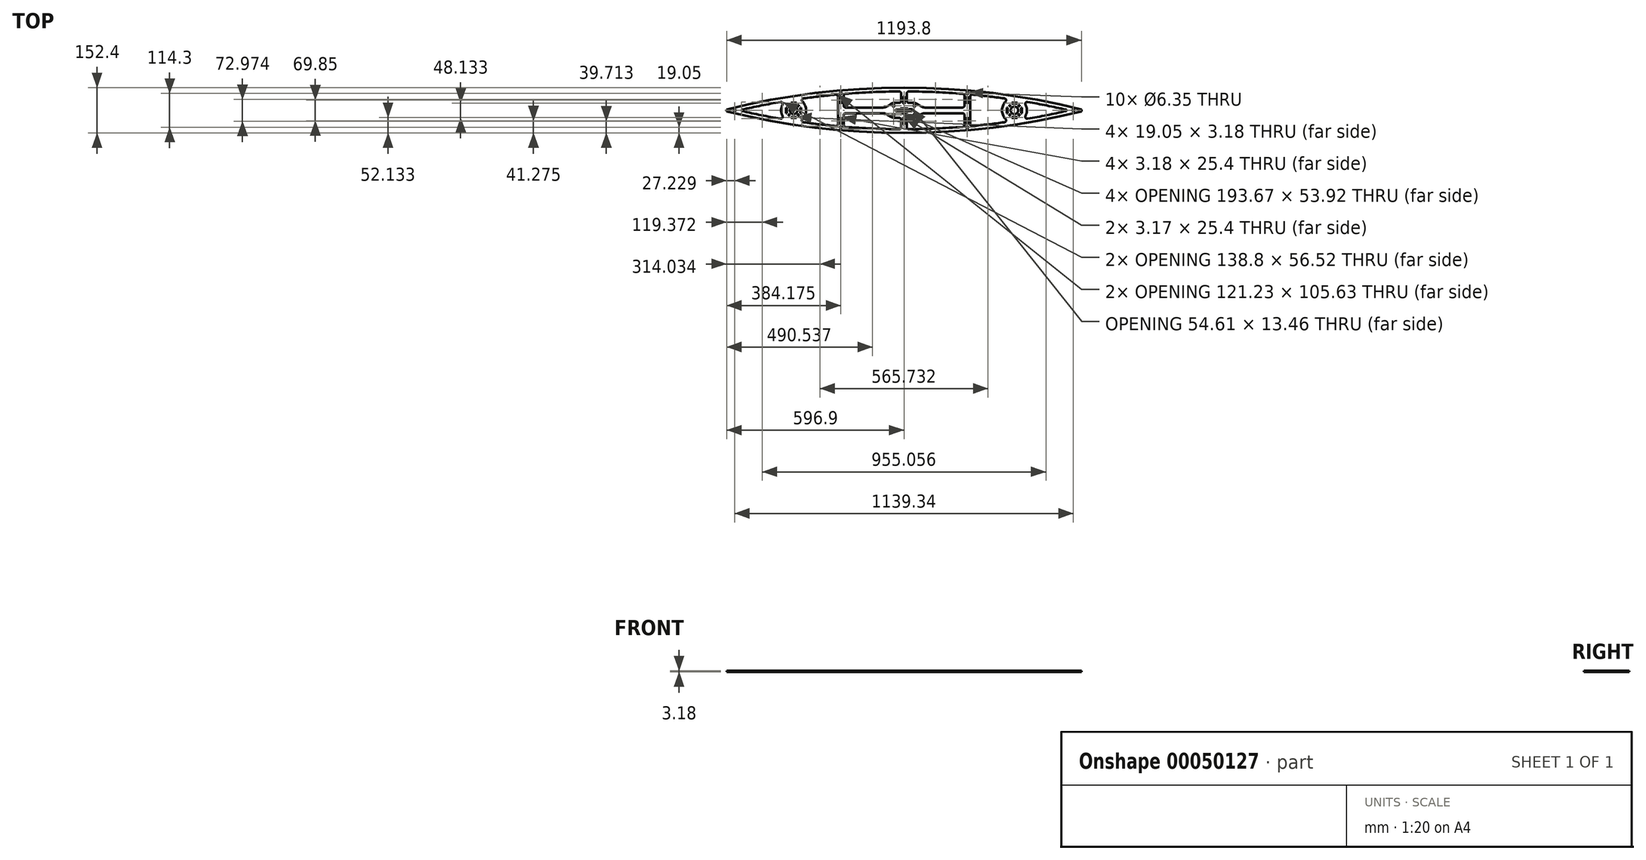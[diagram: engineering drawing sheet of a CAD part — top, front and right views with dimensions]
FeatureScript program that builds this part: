
annotation { "Feature Type Name" : "Feature", "Feature Type Description" : "" }
export const myFeature = defineFeature(function(context is Context, id is Id, definition is map)
    precondition{}
    {
        {
            var Q0;
            Q0=qCreatedBy(makeId("Top.planeOp"),FACE);
            var sketch = newSketch(context, id + "F0", { "sketchPlane" : qUnion([Q0])});
            skArc(sketch, "E0", {"start": v(609.6, 0) * mm, "mid": v(0, 76.2) * mm, "end": v(-609.6, 0) * mm, "construction": true});
            skPoint(sketch, "E1", {"position": v(0, 76.2) * mm});
            skArc(sketch, "E2", {"start": v(596.9, 3.19) * mm, "mid": v(0, 76.2) * mm, "end": v(-596.9, 3.19) * mm});
            skArc(sketch, "E3.0", {"start": v(197.36, 55.58) * mm, "mid": v(106.7, 61.19) * mm, "end": v(15.92, 63.45) * mm});
            skLineSegment(sketch, "E4", {"start": v(-596.9, 3.19) * mm, "end": v(-596.9, 0) * mm});
            skLineSegment(sketch, "E5", {"start": v(596.9, 0) * mm, "end": v(596.9, 3.19) * mm});
            skLineSegment(sketch, "E6", {"start": v(-203.2, 49.25) * mm, "end": v(-203.2, 15.87) * mm});
            skLineSegment(sketch, "E7", {"start": v(-196.85, 9.52) * mm, "end": v(-70.78, 9.52) * mm});
            skLineSegment(sketch, "E8", {"start": v(-57.32, 13.39) * mm, "end": v(-44.28, 21.54) * mm});
            skLineSegment(sketch, "E9", {"start": v(-30.82, 25.4) * mm, "end": v(-15.88, 25.4) * mm});
            skLineSegment(sketch, "E10.MirrorCS", {"start": v(30.82, 25.4) * mm, "end": v(15.88, 25.4) * mm});
            skLineSegment(sketch, "E11.MirrorCS", {"start": v(57.32, 13.39) * mm, "end": v(44.28, 21.54) * mm});
            skLineSegment(sketch, "E12.MirrorCS", {"start": v(203.2, 49.25) * mm, "end": v(203.2, 15.87) * mm});
            skLineSegment(sketch, "E13.MirrorCS", {"start": v(196.85, 9.52) * mm, "end": v(70.78, 9.52) * mm});
            skLineSegment(sketch, "E14.MirrorCS", {"start": v(596.9, 3.19) * mm, "end": v(596.9, 0) * mm});
            skLineSegment(sketch, "E15.MirrorCS", {"start": v(-596.9, -3.19) * mm, "end": v(-596.9, 0) * mm});
            skLineSegment(sketch, "E16.MirrorCS", {"start": v(-203.2, -49.25) * mm, "end": v(-203.2, -15.87) * mm});
            skLineSegment(sketch, "E17.MirrorCS", {"start": v(-196.85, -9.53) * mm, "end": v(-70.78, -9.52) * mm});
            skLineSegment(sketch, "E18.MirrorCS", {"start": v(-57.32, -13.39) * mm, "end": v(-44.28, -21.54) * mm});
            skLineSegment(sketch, "E19.MirrorCS", {"start": v(-30.82, -25.4) * mm, "end": v(-15.88, -25.4) * mm});
            skLineSegment(sketch, "E20.MirrorCS", {"start": v(30.82, -25.4) * mm, "end": v(15.88, -25.4) * mm});
            skLineSegment(sketch, "E21.MirrorCS", {"start": v(57.32, -13.39) * mm, "end": v(44.28, -21.54) * mm});
            skLineSegment(sketch, "E22.MirrorCS", {"start": v(196.85, -9.52) * mm, "end": v(70.78, -9.52) * mm});
            skLineSegment(sketch, "E23.MirrorCS", {"start": v(596.9, -3.19) * mm, "end": v(596.9, 0) * mm});
            skLineSegment(sketch, "E24.MirrorCS", {"start": v(203.2, -49.25) * mm, "end": v(203.2, -15.87) * mm});
            skArc(sketch, "E25.MirrorCS", {"start": v(197.36, -55.58) * mm, "mid": v(106.7, -61.19) * mm, "end": v(15.92, -63.45) * mm});
            skArc(sketch, "E26.MirrorCS", {"start": v(596.9, -3.19) * mm, "mid": v(0, -76.2) * mm, "end": v(-596.9, -3.19) * mm});
            skLineSegment(sketch, "E27.bottom", {"start": v(-27.3, 3.56) * mm, "end": v(27.3, 3.56) * mm, "construction": true});
            skLineSegment(sketch, "E27.top", {"start": v(-27.3, -3.56) * mm, "end": v(27.3, -3.56) * mm, "construction": true});
            skLineSegment(sketch, "E27.left", {"start": v(-27.3, 3.56) * mm, "end": v(-27.3, -3.56) * mm, "construction": true});
            skLineSegment(sketch, "E27.right", {"start": v(27.3, 3.56) * mm, "end": v(27.3, -3.56) * mm, "construction": true});
            skLineSegment(sketch, "E28", {"start": v(-27.3, 0) * mm, "end": v(-27.3, 3.56) * mm});
            skLineSegment(sketch, "E29", {"start": v(-27.3, 3.56) * mm, "end": v(-12.7, 3.56) * mm});
            skLineSegment(sketch, "E30", {"start": v(-12.7, 3.56) * mm, "end": v(-12.7, 6.73) * mm});
            skLineSegment(sketch, "E31", {"start": v(-12.7, 6.73) * mm, "end": v(12.7, 6.73) * mm});
            skLineSegment(sketch, "E32", {"start": v(12.7, 6.73) * mm, "end": v(12.7, 3.56) * mm});
            skLineSegment(sketch, "E33", {"start": v(12.7, 3.56) * mm, "end": v(27.3, 3.56) * mm});
            skLineSegment(sketch, "E34", {"start": v(27.3, 3.56) * mm, "end": v(27.3, 0) * mm});
            skLineSegment(sketch, "E35.MirrorCS", {"start": v(-27.3, 0) * mm, "end": v(-27.3, -3.56) * mm});
            skLineSegment(sketch, "E36.MirrorCS", {"start": v(-27.3, -3.56) * mm, "end": v(-12.7, -3.56) * mm});
            skLineSegment(sketch, "E37.MirrorCS", {"start": v(-12.7, -3.56) * mm, "end": v(-12.7, -6.73) * mm});
            skLineSegment(sketch, "E38.MirrorCS", {"start": v(-12.7, -6.73) * mm, "end": v(12.7, -6.73) * mm});
            skLineSegment(sketch, "E39.MirrorCS", {"start": v(12.7, -6.73) * mm, "end": v(12.7, -3.56) * mm});
            skLineSegment(sketch, "E40.MirrorCS", {"start": v(27.3, -3.56) * mm, "end": v(27.3, 0) * mm});
            skLineSegment(sketch, "E41.MirrorCS", {"start": v(12.7, -3.56) * mm, "end": v(27.3, -3.56) * mm});
            skLineSegment(sketch, "E42", {"start": v(-9.53, 31.75) * mm, "end": v(-9.53, 57.1) * mm});
            skLineSegment(sketch, "E43", {"start": v(9.53, 31.75) * mm, "end": v(9.53, 57.1) * mm});
            skArc(sketch, "E44.trimOffspring", {"start": v(-15.92, 63.45) * mm, "mid": v(-106.7, 61.19) * mm, "end": v(-197.36, 55.58) * mm});
            skPoint(sketch, "E45.orphan", {"position": v(0, 25.4) * mm});
            skLineSegment(sketch, "E46.MirrorCS", {"start": v(9.52, -31.75) * mm, "end": v(9.53, -57.1) * mm});
            skLineSegment(sketch, "E47.MirrorCS", {"start": v(-9.53, -31.75) * mm, "end": v(-9.52, -57.1) * mm});
            skPoint(sketch, "E48.orphan", {"position": v(0, -25.4) * mm});
            skArc(sketch, "E49.trimOffspring", {"start": v(-15.92, -63.45) * mm, "mid": v(-106.7, -61.19) * mm, "end": v(-197.36, -55.58) * mm});
            skPoint(sketch, "E50.visualSharp", {"position": v(-203.2, 55.1) * mm});
            skArc(sketch, "E50.filletArc", {"start": v(-197.36, 55.58) * mm, "mid": v(-201.52, 53.56) * mm, "end": v(-203.2, 49.25) * mm});
            skPoint(sketch, "E51.visualSharp", {"position": v(-203.2, 9.53) * mm});
            skArc(sketch, "E51.filletArc", {"start": v(-203.2, 15.87) * mm, "mid": v(-201.34, 11.38) * mm, "end": v(-196.85, 9.52) * mm});
            skPoint(sketch, "E52.visualSharp", {"position": v(-63.5, 9.52) * mm});
            skArc(sketch, "E52.filletArc", {"start": v(-70.78, 9.52) * mm, "mid": v(-63.78, 10.5) * mm, "end": v(-57.32, 13.39) * mm});
            skPoint(sketch, "E53.visualSharp", {"position": v(-38.1, 25.4) * mm});
            skArc(sketch, "E53.filletArc", {"start": v(-30.82, 25.4) * mm, "mid": v(-37.82, 24.42) * mm, "end": v(-44.28, 21.54) * mm});
            skPoint(sketch, "E54.visualSharp", {"position": v(-38.1, -25.4) * mm});
            skArc(sketch, "E54.filletArc", {"start": v(-44.28, -21.54) * mm, "mid": v(-37.82, -24.42) * mm, "end": v(-30.82, -25.4) * mm});
            skPoint(sketch, "E55.visualSharp", {"position": v(-63.5, -9.52) * mm});
            skArc(sketch, "E55.filletArc", {"start": v(-57.32, -13.39) * mm, "mid": v(-63.78, -10.5) * mm, "end": v(-70.78, -9.52) * mm});
            skPoint(sketch, "E56.visualSharp", {"position": v(-203.2, -9.53) * mm});
            skArc(sketch, "E56.filletArc", {"start": v(-196.85, -9.53) * mm, "mid": v(-201.34, -11.38) * mm, "end": v(-203.2, -15.87) * mm});
            skPoint(sketch, "E57.visualSharp", {"position": v(-203.2, -55.1) * mm});
            skArc(sketch, "E57.filletArc", {"start": v(-203.2, -49.25) * mm, "mid": v(-201.52, -53.56) * mm, "end": v(-197.36, -55.58) * mm});
            skPoint(sketch, "E58.visualSharp", {"position": v(-9.53, -63.48) * mm});
            skArc(sketch, "E58.filletArc", {"start": v(-15.92, -63.45) * mm, "mid": v(-11.4, -61.6) * mm, "end": v(-9.52, -57.1) * mm});
            skPoint(sketch, "E59.visualSharp", {"position": v(-9.53, -25.4) * mm});
            skArc(sketch, "E59.filletArc", {"start": v(-9.52, -31.75) * mm, "mid": v(-11.38, -27.26) * mm, "end": v(-15.88, -25.4) * mm});
            skPoint(sketch, "E60.visualSharp", {"position": v(-9.53, 25.4) * mm});
            skArc(sketch, "E60.filletArc", {"start": v(-15.88, 25.4) * mm, "mid": v(-11.38, 27.26) * mm, "end": v(-9.52, 31.75) * mm});
            skPoint(sketch, "E61.visualSharp", {"position": v(-9.53, 63.48) * mm});
            skArc(sketch, "E61.filletArc", {"start": v(-9.52, 57.1) * mm, "mid": v(-11.4, 61.6) * mm, "end": v(-15.92, 63.45) * mm});
            skPoint(sketch, "E62.visualSharp", {"position": v(9.53, 63.48) * mm});
            skArc(sketch, "E62.filletArc", {"start": v(15.92, 63.45) * mm, "mid": v(11.4, 61.6) * mm, "end": v(9.53, 57.1) * mm});
            skPoint(sketch, "E63.visualSharp", {"position": v(9.53, 25.4) * mm});
            skArc(sketch, "E63.filletArc", {"start": v(9.52, 31.75) * mm, "mid": v(11.38, 27.26) * mm, "end": v(15.88, 25.4) * mm});
            skPoint(sketch, "E64.visualSharp", {"position": v(38.1, 25.4) * mm});
            skArc(sketch, "E64.filletArc", {"start": v(44.28, 21.54) * mm, "mid": v(37.82, 24.42) * mm, "end": v(30.82, 25.4) * mm});
            skPoint(sketch, "E65.visualSharp", {"position": v(63.5, 9.52) * mm});
            skArc(sketch, "E65.filletArc", {"start": v(57.32, 13.39) * mm, "mid": v(63.78, 10.5) * mm, "end": v(70.78, 9.52) * mm});
            skPoint(sketch, "E66.visualSharp", {"position": v(63.5, -9.52) * mm});
            skArc(sketch, "E66.filletArc", {"start": v(70.78, -9.52) * mm, "mid": v(63.78, -10.5) * mm, "end": v(57.32, -13.39) * mm});
            skPoint(sketch, "E67.visualSharp", {"position": v(38.1, -25.4) * mm});
            skArc(sketch, "E67.filletArc", {"start": v(30.82, -25.4) * mm, "mid": v(37.82, -24.42) * mm, "end": v(44.28, -21.54) * mm});
            skPoint(sketch, "E68.visualSharp", {"position": v(9.53, -25.4) * mm});
            skArc(sketch, "E68.filletArc", {"start": v(15.88, -25.4) * mm, "mid": v(11.38, -27.26) * mm, "end": v(9.52, -31.75) * mm});
            skPoint(sketch, "E69.visualSharp", {"position": v(9.53, -63.48) * mm});
            skArc(sketch, "E69.filletArc", {"start": v(9.53, -57.1) * mm, "mid": v(11.4, -61.6) * mm, "end": v(15.92, -63.45) * mm});
            skPoint(sketch, "E70.visualSharp", {"position": v(203.2, 55.1) * mm});
            skArc(sketch, "E70.filletArc", {"start": v(203.2, 49.25) * mm, "mid": v(201.52, 53.56) * mm, "end": v(197.36, 55.58) * mm});
            skPoint(sketch, "E71.visualSharp", {"position": v(203.2, 9.53) * mm});
            skArc(sketch, "E71.filletArc", {"start": v(196.85, 9.52) * mm, "mid": v(201.34, 11.38) * mm, "end": v(203.2, 15.87) * mm});
            skPoint(sketch, "E72.visualSharp", {"position": v(203.2, -9.53) * mm});
            skArc(sketch, "E72.filletArc", {"start": v(203.2, -15.87) * mm, "mid": v(201.34, -11.38) * mm, "end": v(196.85, -9.52) * mm});
            skPoint(sketch, "E73.visualSharp", {"position": v(203.2, -55.1) * mm});
            skArc(sketch, "E73.filletArc", {"start": v(197.36, -55.58) * mm, "mid": v(201.52, -53.56) * mm, "end": v(203.2, -49.25) * mm});
            skLineSegment(sketch, "E74", {"start": v(-222.25, 46.5) * mm, "end": v(-222.25, 0) * mm});
            skArc(sketch, "E75", {"start": v(-229.2, 52.82) * mm, "mid": v(-283.67, 47.12) * mm, "end": v(-338.01, 40.2) * mm});
            skArc(sketch, "E76", {"start": v(-329.57, 0) * mm, "mid": v(-332.7, 15.92) * mm, "end": v(-341.66, 29.45) * mm});
            skPoint(sketch, "E77.visualSharp", {"position": v(-222.25, 53.46) * mm});
            skArc(sketch, "E77.filletArc", {"start": v(-222.25, 46.5) * mm, "mid": v(-224.32, 51.19) * mm, "end": v(-229.2, 52.82) * mm});
            skPoint(sketch, "E78.end.orphan", {"position": v(-361.95, 36.77) * mm});
            skPoint(sketch, "E79.visualSharp", {"position": v(-353.74, 37.97) * mm});
            skArc(sketch, "E79.filletArc", {"start": v(-338.01, 40.2) * mm, "mid": v(-343.15, 35.95) * mm, "end": v(-341.66, 29.45) * mm});
            skCircle(sketch, "E80", {"center": v(-371.48, 0) * mm, "radius": 41.91 * mm, "construction": true});
            skArc(sketch, "E81.MirrorCS", {"start": v(-329.57, 0) * mm, "mid": v(-332.7, -15.92) * mm, "end": v(-341.66, -29.45) * mm});
            skArc(sketch, "E82.MirrorCS", {"start": v(-338.01, -40.2) * mm, "mid": v(-343.15, -35.95) * mm, "end": v(-341.66, -29.45) * mm});
            skArc(sketch, "E83.MirrorCS", {"start": v(-229.2, -52.82) * mm, "mid": v(-283.67, -47.12) * mm, "end": v(-338.01, -40.2) * mm});
            skArc(sketch, "E84.MirrorCS", {"start": v(-222.25, -46.5) * mm, "mid": v(-224.32, -51.19) * mm, "end": v(-229.2, -52.82) * mm});
            skLineSegment(sketch, "E85.MirrorCS", {"start": v(-222.25, -46.5) * mm, "end": v(-222.25, 0) * mm});
            skArc(sketch, "E86.MirrorCS", {"start": v(338.01, 40.2) * mm, "mid": v(343.15, 35.95) * mm, "end": v(341.66, 29.45) * mm});
            skArc(sketch, "E87.MirrorCS", {"start": v(329.57, 0) * mm, "mid": v(332.7, 15.92) * mm, "end": v(341.66, 29.45) * mm});
            skArc(sketch, "E88.MirrorCS", {"start": v(329.57, 0) * mm, "mid": v(332.7, -15.92) * mm, "end": v(341.66, -29.45) * mm});
            skArc(sketch, "E89.MirrorCS", {"start": v(338.01, -40.2) * mm, "mid": v(343.15, -35.95) * mm, "end": v(341.66, -29.45) * mm});
            skArc(sketch, "E90.MirrorCS", {"start": v(229.2, -52.82) * mm, "mid": v(283.67, -47.12) * mm, "end": v(338.01, -40.2) * mm});
            skArc(sketch, "E91.MirrorCS", {"start": v(222.25, -46.5) * mm, "mid": v(224.32, -51.19) * mm, "end": v(229.2, -52.82) * mm});
            skLineSegment(sketch, "E92.MirrorCS", {"start": v(222.25, -46.5) * mm, "end": v(222.25, 0) * mm});
            skLineSegment(sketch, "E93.MirrorCS", {"start": v(222.25, 46.5) * mm, "end": v(222.25, 0) * mm});
            skArc(sketch, "E94.MirrorCS", {"start": v(222.25, 46.5) * mm, "mid": v(224.32, 51.19) * mm, "end": v(229.2, 52.82) * mm});
            skArc(sketch, "E95.MirrorCS", {"start": v(229.2, 52.82) * mm, "mid": v(283.67, 47.12) * mm, "end": v(338.01, 40.2) * mm});
            skCircle(sketch, "E96.MirrorC", {"center": v(371.48, 0) * mm, "radius": 41.91 * mm, "construction": true});
            skArc(sketch, "E97", {"start": v(-415.53, 28.2) * mm, "mid": v(-480.41, 16.2) * mm, "end": v(-544.95, 2.48) * mm});
            skArc(sketch, "E98", {"start": v(-408.8, 19.06) * mm, "mid": v(-412.22, 9.8) * mm, "end": v(-413.38, 0) * mm});
            skPoint(sketch, "E99.visualSharp", {"position": v(-399.86, 30.84) * mm});
            skArc(sketch, "E99.filletArc", {"start": v(-408.8, 19.06) * mm, "mid": v(-409.34, 25.71) * mm, "end": v(-415.53, 28.2) * mm});
            skArc(sketch, "E100.MirrorCS", {"start": v(-415.53, -28.2) * mm, "mid": v(-480.41, -16.2) * mm, "end": v(-544.95, -2.48) * mm});
            skArc(sketch, "E101.MirrorCS", {"start": v(-408.8, -19.06) * mm, "mid": v(-409.34, -25.71) * mm, "end": v(-415.53, -28.2) * mm});
            skArc(sketch, "E102.MirrorCS", {"start": v(-408.8, -19.06) * mm, "mid": v(-412.22, -9.8) * mm, "end": v(-413.38, 0) * mm});
            skPoint(sketch, "E103.visualSharp", {"position": v(-555.76, 0) * mm});
            skArc(sketch, "E103.filletArc", {"start": v(-544.95, 2.48) * mm, "mid": v(-546.93, 0) * mm, "end": v(-544.95, -2.48) * mm});
            skArc(sketch, "E104.MirrorCS", {"start": v(544.95, 2.48) * mm, "mid": v(546.93, 0) * mm, "end": v(544.95, -2.48) * mm});
            skArc(sketch, "E105.MirrorCS", {"start": v(415.53, -28.2) * mm, "mid": v(480.41, -16.2) * mm, "end": v(544.95, -2.48) * mm});
            skArc(sketch, "E106.MirrorCS", {"start": v(415.53, 28.2) * mm, "mid": v(480.41, 16.2) * mm, "end": v(544.95, 2.48) * mm});
            skArc(sketch, "E107.MirrorCS", {"start": v(408.8, 19.06) * mm, "mid": v(409.34, 25.71) * mm, "end": v(415.53, 28.2) * mm});
            skArc(sketch, "E108.MirrorCS", {"start": v(408.8, 19.06) * mm, "mid": v(412.22, 9.8) * mm, "end": v(413.38, 0) * mm});
            skArc(sketch, "E109.MirrorCS", {"start": v(408.8, -19.06) * mm, "mid": v(412.22, -9.8) * mm, "end": v(413.38, 0) * mm});
            skArc(sketch, "E110.MirrorCS", {"start": v(408.8, -19.06) * mm, "mid": v(409.34, -25.71) * mm, "end": v(415.53, -28.2) * mm});
            skCircle(sketch, "E111", {"center": v(-212.73, 57.15) * mm, "radius": 3.18 * mm});
            skCircle(sketch, "E112", {"center": v(-34.92, 15.24) * mm, "radius": 3.18 * mm});
            skCircle(sketch, "E113.MirrorC", {"center": v(-34.92, -15.24) * mm, "radius": 3.18 * mm});
            skCircle(sketch, "E114.MirrorC", {"center": v(-212.73, -57.15) * mm, "radius": 3.18 * mm});
            skCircle(sketch, "E115.MirrorC", {"center": v(212.73, 57.15) * mm, "radius": 3.18 * mm});
            skCircle(sketch, "E116.MirrorC", {"center": v(212.73, -57.15) * mm, "radius": 3.18 * mm});
            skCircle(sketch, "E117.MirrorC", {"center": v(34.92, 15.24) * mm, "radius": 3.18 * mm});
            skCircle(sketch, "E118.MirrorC", {"center": v(34.92, -15.24) * mm, "radius": 3.18 * mm});
            skCircle(sketch, "E119", {"center": v(-569.67, 0) * mm, "radius": 3.18 * mm});
            skCircle(sketch, "E120.MirrorC", {"center": v(569.67, 0) * mm, "radius": 3.18 * mm});
            skPoint(sketch, "E121", {"position": v(0, -76.2) * mm});
            skSolve(sketch);
        }
        {
            var Q0;
            Q0=makeQuery(id+"F0.imprint","IMPRINT",FACE,{"disambiguationData":[TD([[makeQuery(id+"F0.imprint","IMPRINT",EDGE,{"derivedFrom":sQuery(id+"F0.wireOp",EDGE,"E2")}),1.0]])]});
            extrude(context, id + "F1", {"entities" : qUnion([Q0]), "depth" : 3.17 * mm});
        }
        {
            var Q0;
            Q0=makeQuery(id+"F1.opExtrude","CAP_FACE",FACE,{"disambiguationData":[OSD([sQuery(id+"F0.wireOp",EDGE,"E2"),sQuery(id+"F0.wireOp",EDGE,"E3.0"),sQuery(id+"F0.wireOp",EDGE,"E4"),sQuery(id+"F0.wireOp",EDGE,"E6"),sQuery(id+"F0.wireOp",EDGE,"E7"),sQuery(id+"F0.wireOp",EDGE,"E8"),sQuery(id+"F0.wireOp",EDGE,"E9"),sQuery(id+"F0.wireOp",EDGE,"E10.MirrorCS"),sQuery(id+"F0.wireOp",EDGE,"E11.MirrorCS"),sQuery(id+"F0.wireOp",EDGE,"E12.MirrorCS"),sQuery(id+"F0.wireOp",EDGE,"E13.MirrorCS"),sQuery(id+"F0.wireOp",EDGE,"E14.MirrorCS"),sQuery(id+"F0.wireOp",EDGE,"E15.MirrorCS"),sQuery(id+"F0.wireOp",EDGE,"E16.MirrorCS"),sQuery(id+"F0.wireOp",EDGE,"E17.MirrorCS"),sQuery(id+"F0.wireOp",EDGE,"E18.MirrorCS"),sQuery(id+"F0.wireOp",EDGE,"E19.MirrorCS"),sQuery(id+"F0.wireOp",EDGE,"E20.MirrorCS"),sQuery(id+"F0.wireOp",EDGE,"E21.MirrorCS"),sQuery(id+"F0.wireOp",EDGE,"E22.MirrorCS"),sQuery(id+"F0.wireOp",EDGE,"E23.MirrorCS"),sQuery(id+"F0.wireOp",EDGE,"E24.MirrorCS"),sQuery(id+"F0.wireOp",EDGE,"E25.MirrorCS"),sQuery(id+"F0.wireOp",EDGE,"E26.MirrorCS"),sQuery(id+"F0.wireOp",EDGE,"E28"),sQuery(id+"F0.wireOp",EDGE,"E29"),sQuery(id+"F0.wireOp",EDGE,"E30"),sQuery(id+"F0.wireOp",EDGE,"E31"),sQuery(id+"F0.wireOp",EDGE,"E32"),sQuery(id+"F0.wireOp",EDGE,"E33"),sQuery(id+"F0.wireOp",EDGE,"E34"),sQuery(id+"F0.wireOp",EDGE,"E35.MirrorCS"),sQuery(id+"F0.wireOp",EDGE,"E36.MirrorCS"),sQuery(id+"F0.wireOp",EDGE,"E37.MirrorCS"),sQuery(id+"F0.wireOp",EDGE,"E38.MirrorCS"),sQuery(id+"F0.wireOp",EDGE,"E39.MirrorCS"),sQuery(id+"F0.wireOp",EDGE,"E40.MirrorCS"),sQuery(id+"F0.wireOp",EDGE,"E41.MirrorCS"),sQuery(id+"F0.wireOp",EDGE,"E42"),sQuery(id+"F0.wireOp",EDGE,"E43"),sQuery(id+"F0.wireOp",EDGE,"E44.trimOffspring"),sQuery(id+"F0.wireOp",EDGE,"E46.MirrorCS"),sQuery(id+"F0.wireOp",EDGE,"E47.MirrorCS"),sQuery(id+"F0.wireOp",EDGE,"E49.trimOffspring"),sQuery(id+"F0.wireOp",EDGE,"E50.filletArc"),sQuery(id+"F0.wireOp",EDGE,"E51.filletArc"),sQuery(id+"F0.wireOp",EDGE,"E52.filletArc"),sQuery(id+"F0.wireOp",EDGE,"E53.filletArc"),sQuery(id+"F0.wireOp",EDGE,"E54.filletArc"),sQuery(id+"F0.wireOp",EDGE,"E55.filletArc"),sQuery(id+"F0.wireOp",EDGE,"E56.filletArc"),sQuery(id+"F0.wireOp",EDGE,"E57.filletArc"),sQuery(id+"F0.wireOp",EDGE,"E58.filletArc"),sQuery(id+"F0.wireOp",EDGE,"E59.filletArc"),sQuery(id+"F0.wireOp",EDGE,"E60.filletArc"),sQuery(id+"F0.wireOp",EDGE,"E61.filletArc"),sQuery(id+"F0.wireOp",EDGE,"E62.filletArc"),sQuery(id+"F0.wireOp",EDGE,"E63.filletArc"),sQuery(id+"F0.wireOp",EDGE,"E64.filletArc"),sQuery(id+"F0.wireOp",EDGE,"E65.filletArc"),sQuery(id+"F0.wireOp",EDGE,"E66.filletArc"),sQuery(id+"F0.wireOp",EDGE,"E67.filletArc"),sQuery(id+"F0.wireOp",EDGE,"E68.filletArc"),sQuery(id+"F0.wireOp",EDGE,"E69.filletArc"),sQuery(id+"F0.wireOp",EDGE,"E70.filletArc"),sQuery(id+"F0.wireOp",EDGE,"E71.filletArc"),sQuery(id+"F0.wireOp",EDGE,"E72.filletArc"),sQuery(id+"F0.wireOp",EDGE,"E73.filletArc"),sQuery(id+"F0.wireOp",EDGE,"E74"),sQuery(id+"F0.wireOp",EDGE,"E75"),sQuery(id+"F0.wireOp",EDGE,"E76"),sQuery(id+"F0.wireOp",EDGE,"E77.filletArc"),sQuery(id+"F0.wireOp",EDGE,"E79.filletArc"),sQuery(id+"F0.wireOp",EDGE,"E81.MirrorCS"),sQuery(id+"F0.wireOp",EDGE,"E82.MirrorCS"),sQuery(id+"F0.wireOp",EDGE,"E83.MirrorCS"),sQuery(id+"F0.wireOp",EDGE,"E84.MirrorCS"),sQuery(id+"F0.wireOp",EDGE,"E85.MirrorCS"),sQuery(id+"F0.wireOp",EDGE,"E86.MirrorCS"),sQuery(id+"F0.wireOp",EDGE,"E87.MirrorCS"),sQuery(id+"F0.wireOp",EDGE,"E88.MirrorCS"),sQuery(id+"F0.wireOp",EDGE,"E89.MirrorCS"),sQuery(id+"F0.wireOp",EDGE,"E90.MirrorCS"),sQuery(id+"F0.wireOp",EDGE,"E91.MirrorCS"),sQuery(id+"F0.wireOp",EDGE,"E92.MirrorCS"),sQuery(id+"F0.wireOp",EDGE,"E93.MirrorCS"),sQuery(id+"F0.wireOp",EDGE,"E94.MirrorCS"),sQuery(id+"F0.wireOp",EDGE,"E95.MirrorCS"),sQuery(id+"F0.wireOp",EDGE,"E97"),sQuery(id+"F0.wireOp",EDGE,"E98"),sQuery(id+"F0.wireOp",EDGE,"E99.filletArc"),sQuery(id+"F0.wireOp",EDGE,"E100.MirrorCS"),sQuery(id+"F0.wireOp",EDGE,"E101.MirrorCS"),sQuery(id+"F0.wireOp",EDGE,"E102.MirrorCS"),sQuery(id+"F0.wireOp",EDGE,"E103.filletArc"),sQuery(id+"F0.wireOp",EDGE,"E104.MirrorCS"),sQuery(id+"F0.wireOp",EDGE,"E105.MirrorCS"),sQuery(id+"F0.wireOp",EDGE,"E106.MirrorCS"),sQuery(id+"F0.wireOp",EDGE,"E107.MirrorCS"),sQuery(id+"F0.wireOp",EDGE,"E108.MirrorCS"),sQuery(id+"F0.wireOp",EDGE,"E109.MirrorCS"),sQuery(id+"F0.wireOp",EDGE,"E110.MirrorCS")])],"isStart":false});
            var sketch = newSketch(context, id + "F2", { "sketchPlane" : qUnion([Q0])});
            skLineSegment(sketch, "E122.bottom", {"start": v(-214.31, 47.62) * mm, "end": v(-211.14, 47.62) * mm});
            skLineSegment(sketch, "E122.top", {"start": v(-214.31, 22.23) * mm, "end": v(-211.14, 22.23) * mm});
            skLineSegment(sketch, "E122.left", {"start": v(-214.31, 47.62) * mm, "end": v(-214.31, 22.23) * mm});
            skLineSegment(sketch, "E122.right", {"start": v(-211.14, 47.62) * mm, "end": v(-211.14, 22.23) * mm});
            skLineSegment(sketch, "E123.bottom", {"start": v(-1.59, 47.63) * mm, "end": v(1.59, 47.63) * mm});
            skLineSegment(sketch, "E123.top", {"start": v(-1.59, 22.23) * mm, "end": v(1.59, 22.23) * mm});
            skLineSegment(sketch, "E123.left", {"start": v(-1.59, 47.63) * mm, "end": v(-1.59, 22.23) * mm});
            skLineSegment(sketch, "E123.right", {"start": v(1.59, 47.63) * mm, "end": v(1.59, 22.23) * mm});
            skPoint(sketch, "E124", {"position": v(0, 47.63) * mm});
            skLineSegment(sketch, "E125", {"start": v(-222.25, 0) * mm, "end": v(-203.2, 0) * mm, "construction": true});
            skPoint(sketch, "E125.endSnap0", {"position": v(-222.25, 0) * mm});
            skLineSegment(sketch, "E126", {"start": v(-212.73, 22.23) * mm, "end": v(-212.73, 0) * mm, "construction": true});
            skLineSegment(sketch, "E127.MirrorCS", {"start": v(211.14, 47.62) * mm, "end": v(211.14, 22.23) * mm});
            skLineSegment(sketch, "E128.MirrorCS", {"start": v(214.31, 47.63) * mm, "end": v(211.14, 47.63) * mm});
            skLineSegment(sketch, "E129.MirrorCS", {"start": v(214.31, 47.62) * mm, "end": v(214.31, 22.23) * mm});
            skLineSegment(sketch, "E130.MirrorCS", {"start": v(214.31, 22.23) * mm, "end": v(211.14, 22.23) * mm});
            skLineSegment(sketch, "E131.MirrorCS", {"start": v(214.31, -47.62) * mm, "end": v(214.31, -22.23) * mm});
            skLineSegment(sketch, "E132.MirrorCS", {"start": v(214.31, -47.63) * mm, "end": v(211.14, -47.63) * mm});
            skLineSegment(sketch, "E133.MirrorCS", {"start": v(211.14, -47.62) * mm, "end": v(211.14, -22.23) * mm});
            skLineSegment(sketch, "E134.MirrorCS", {"start": v(214.31, -22.23) * mm, "end": v(211.14, -22.23) * mm});
            skLineSegment(sketch, "E135.MirrorCS", {"start": v(1.59, -47.63) * mm, "end": v(1.59, -22.23) * mm});
            skLineSegment(sketch, "E136.MirrorCS", {"start": v(-1.59, -22.23) * mm, "end": v(1.59, -22.23) * mm});
            skLineSegment(sketch, "E137.MirrorCS", {"start": v(-1.59, -47.63) * mm, "end": v(-1.59, -22.23) * mm});
            skLineSegment(sketch, "E138.MirrorCS", {"start": v(-1.59, -47.63) * mm, "end": v(1.59, -47.63) * mm});
            skLineSegment(sketch, "E139.MirrorCS", {"start": v(-211.14, -47.62) * mm, "end": v(-211.14, -22.23) * mm});
            skLineSegment(sketch, "E140.MirrorCS", {"start": v(-214.31, -47.62) * mm, "end": v(-214.31, -22.23) * mm});
            skLineSegment(sketch, "E141.MirrorCS", {"start": v(-214.31, -22.23) * mm, "end": v(-211.14, -22.23) * mm});
            skLineSegment(sketch, "E142.MirrorCS", {"start": v(-214.31, -47.63) * mm, "end": v(-211.14, -47.63) * mm});
            skPoint(sketch, "E143", {"position": v(211.14, 67.18) * mm});
            skPoint(sketch, "E144", {"position": v(211.14, -67.18) * mm});
            skSolve(sketch);
        }
        {
            var Q0;
            Q0 = qSketchRegion(id + "F2", true);
            extrude(context, id + "F3", {"entities" : qUnion([Q0]), "operationType" : NewBodyOperationType.REMOVE, "endBound" : BoundingType.THROUGH_ALL, "oppositeDirection" : true, "depth" : 25.4 * mm});
        }
        {
            var Q0;
            Q0=makeQuery(id+"F1.opExtrude","CAP_FACE",FACE,{"disambiguationData":[OSD([sQuery(id+"F0.wireOp",EDGE,"E2"),sQuery(id+"F0.wireOp",EDGE,"E3.0"),sQuery(id+"F0.wireOp",EDGE,"E4"),sQuery(id+"F0.wireOp",EDGE,"E6"),sQuery(id+"F0.wireOp",EDGE,"E7"),sQuery(id+"F0.wireOp",EDGE,"E8"),sQuery(id+"F0.wireOp",EDGE,"E9"),sQuery(id+"F0.wireOp",EDGE,"E10.MirrorCS"),sQuery(id+"F0.wireOp",EDGE,"E11.MirrorCS"),sQuery(id+"F0.wireOp",EDGE,"E12.MirrorCS"),sQuery(id+"F0.wireOp",EDGE,"E13.MirrorCS"),sQuery(id+"F0.wireOp",EDGE,"E14.MirrorCS"),sQuery(id+"F0.wireOp",EDGE,"E15.MirrorCS"),sQuery(id+"F0.wireOp",EDGE,"E16.MirrorCS"),sQuery(id+"F0.wireOp",EDGE,"E17.MirrorCS"),sQuery(id+"F0.wireOp",EDGE,"E18.MirrorCS"),sQuery(id+"F0.wireOp",EDGE,"E19.MirrorCS"),sQuery(id+"F0.wireOp",EDGE,"E20.MirrorCS"),sQuery(id+"F0.wireOp",EDGE,"E21.MirrorCS"),sQuery(id+"F0.wireOp",EDGE,"E22.MirrorCS"),sQuery(id+"F0.wireOp",EDGE,"E23.MirrorCS"),sQuery(id+"F0.wireOp",EDGE,"E24.MirrorCS"),sQuery(id+"F0.wireOp",EDGE,"E25.MirrorCS"),sQuery(id+"F0.wireOp",EDGE,"E26.MirrorCS"),sQuery(id+"F0.wireOp",EDGE,"E28"),sQuery(id+"F0.wireOp",EDGE,"E29"),sQuery(id+"F0.wireOp",EDGE,"E30"),sQuery(id+"F0.wireOp",EDGE,"E31"),sQuery(id+"F0.wireOp",EDGE,"E32"),sQuery(id+"F0.wireOp",EDGE,"E33"),sQuery(id+"F0.wireOp",EDGE,"E34"),sQuery(id+"F0.wireOp",EDGE,"E35.MirrorCS"),sQuery(id+"F0.wireOp",EDGE,"E36.MirrorCS"),sQuery(id+"F0.wireOp",EDGE,"E37.MirrorCS"),sQuery(id+"F0.wireOp",EDGE,"E38.MirrorCS"),sQuery(id+"F0.wireOp",EDGE,"E39.MirrorCS"),sQuery(id+"F0.wireOp",EDGE,"E40.MirrorCS"),sQuery(id+"F0.wireOp",EDGE,"E41.MirrorCS"),sQuery(id+"F0.wireOp",EDGE,"E42"),sQuery(id+"F0.wireOp",EDGE,"E43"),sQuery(id+"F0.wireOp",EDGE,"E44.trimOffspring"),sQuery(id+"F0.wireOp",EDGE,"E46.MirrorCS"),sQuery(id+"F0.wireOp",EDGE,"E47.MirrorCS"),sQuery(id+"F0.wireOp",EDGE,"E49.trimOffspring"),sQuery(id+"F0.wireOp",EDGE,"E50.filletArc"),sQuery(id+"F0.wireOp",EDGE,"E51.filletArc"),sQuery(id+"F0.wireOp",EDGE,"E52.filletArc"),sQuery(id+"F0.wireOp",EDGE,"E53.filletArc"),sQuery(id+"F0.wireOp",EDGE,"E54.filletArc"),sQuery(id+"F0.wireOp",EDGE,"E55.filletArc"),sQuery(id+"F0.wireOp",EDGE,"E56.filletArc"),sQuery(id+"F0.wireOp",EDGE,"E57.filletArc"),sQuery(id+"F0.wireOp",EDGE,"E58.filletArc"),sQuery(id+"F0.wireOp",EDGE,"E59.filletArc"),sQuery(id+"F0.wireOp",EDGE,"E60.filletArc"),sQuery(id+"F0.wireOp",EDGE,"E61.filletArc"),sQuery(id+"F0.wireOp",EDGE,"E62.filletArc"),sQuery(id+"F0.wireOp",EDGE,"E63.filletArc"),sQuery(id+"F0.wireOp",EDGE,"E64.filletArc"),sQuery(id+"F0.wireOp",EDGE,"E65.filletArc"),sQuery(id+"F0.wireOp",EDGE,"E66.filletArc"),sQuery(id+"F0.wireOp",EDGE,"E67.filletArc"),sQuery(id+"F0.wireOp",EDGE,"E68.filletArc"),sQuery(id+"F0.wireOp",EDGE,"E69.filletArc"),sQuery(id+"F0.wireOp",EDGE,"E70.filletArc"),sQuery(id+"F0.wireOp",EDGE,"E71.filletArc"),sQuery(id+"F0.wireOp",EDGE,"E72.filletArc"),sQuery(id+"F0.wireOp",EDGE,"E73.filletArc"),sQuery(id+"F0.wireOp",EDGE,"E74"),sQuery(id+"F0.wireOp",EDGE,"E75"),sQuery(id+"F0.wireOp",EDGE,"E76"),sQuery(id+"F0.wireOp",EDGE,"E77.filletArc"),sQuery(id+"F0.wireOp",EDGE,"E79.filletArc"),sQuery(id+"F0.wireOp",EDGE,"E81.MirrorCS"),sQuery(id+"F0.wireOp",EDGE,"E82.MirrorCS"),sQuery(id+"F0.wireOp",EDGE,"E83.MirrorCS"),sQuery(id+"F0.wireOp",EDGE,"E84.MirrorCS"),sQuery(id+"F0.wireOp",EDGE,"E85.MirrorCS"),sQuery(id+"F0.wireOp",EDGE,"E86.MirrorCS"),sQuery(id+"F0.wireOp",EDGE,"E87.MirrorCS"),sQuery(id+"F0.wireOp",EDGE,"E88.MirrorCS"),sQuery(id+"F0.wireOp",EDGE,"E89.MirrorCS"),sQuery(id+"F0.wireOp",EDGE,"E90.MirrorCS"),sQuery(id+"F0.wireOp",EDGE,"E91.MirrorCS"),sQuery(id+"F0.wireOp",EDGE,"E92.MirrorCS"),sQuery(id+"F0.wireOp",EDGE,"E93.MirrorCS"),sQuery(id+"F0.wireOp",EDGE,"E94.MirrorCS"),sQuery(id+"F0.wireOp",EDGE,"E95.MirrorCS"),sQuery(id+"F0.wireOp",EDGE,"E97"),sQuery(id+"F0.wireOp",EDGE,"E98"),sQuery(id+"F0.wireOp",EDGE,"E99.filletArc"),sQuery(id+"F0.wireOp",EDGE,"E100.MirrorCS"),sQuery(id+"F0.wireOp",EDGE,"E101.MirrorCS"),sQuery(id+"F0.wireOp",EDGE,"E102.MirrorCS"),sQuery(id+"F0.wireOp",EDGE,"E103.filletArc"),sQuery(id+"F0.wireOp",EDGE,"E104.MirrorCS"),sQuery(id+"F0.wireOp",EDGE,"E105.MirrorCS"),sQuery(id+"F0.wireOp",EDGE,"E106.MirrorCS"),sQuery(id+"F0.wireOp",EDGE,"E107.MirrorCS"),sQuery(id+"F0.wireOp",EDGE,"E108.MirrorCS"),sQuery(id+"F0.wireOp",EDGE,"E109.MirrorCS"),sQuery(id+"F0.wireOp",EDGE,"E110.MirrorCS")])],"isStart":false});
            var sketch = newSketch(context, id + "F4", { "sketchPlane" : qUnion([Q0])});
            skLineSegment(sketch, "E145", {"start": v(-371.48, 0) * mm, "end": v(-371.48, 48.18) * mm, "construction": true});
            skLineSegment(sketch, "E146", {"start": v(-371.48, 0) * mm, "end": v(-371.48, -48.18) * mm, "construction": true});
            skLineSegment(sketch, "E147.bottom", {"start": v(-393.95, 22.48) * mm, "end": v(-349, 22.48) * mm, "construction": true});
            skLineSegment(sketch, "E147.top", {"start": v(-393.95, -22.48) * mm, "end": v(-349, -22.48) * mm, "construction": true});
            skLineSegment(sketch, "E147.left", {"start": v(-393.95, 22.48) * mm, "end": v(-393.95, -22.48) * mm, "construction": true});
            skLineSegment(sketch, "E147.right", {"start": v(-349, 22.48) * mm, "end": v(-349, -22.48) * mm, "construction": true});
            skLineSegment(sketch, "E148", {"start": v(-413.38, 0) * mm, "end": v(-329.57, 0) * mm, "construction": true});
            skPoint(sketch, "E149", {"position": v(-371.48, 22.48) * mm});
            skPoint(sketch, "E150", {"position": v(-393.95, 0) * mm});
            skLineSegment(sketch, "E151.bottom", {"start": v(-381, 22.48) * mm, "end": v(-361.95, 22.48) * mm});
            skLineSegment(sketch, "E151.top", {"start": v(-381, 25.65) * mm, "end": v(-361.95, 25.65) * mm});
            skLineSegment(sketch, "E151.left", {"start": v(-381, 22.48) * mm, "end": v(-381, 25.65) * mm});
            skLineSegment(sketch, "E151.right", {"start": v(-361.95, 22.48) * mm, "end": v(-361.95, 25.65) * mm});
            skLineSegment(sketch, "E152.bottom", {"start": v(-393.95, 9.53) * mm, "end": v(-397.13, 9.53) * mm});
            skLineSegment(sketch, "E152.top", {"start": v(-393.95, -9.53) * mm, "end": v(-397.13, -9.53) * mm});
            skLineSegment(sketch, "E152.left", {"start": v(-393.95, 9.52) * mm, "end": v(-393.95, -9.52) * mm});
            skLineSegment(sketch, "E152.right", {"start": v(-397.13, 9.53) * mm, "end": v(-397.13, -9.53) * mm});
            skPoint(sketch, "E153", {"position": v(-397.13, 0) * mm});
            skPoint(sketch, "E154", {"position": v(-371.48, 25.65) * mm});
            skLineSegment(sketch, "E155.MirrorCS", {"start": v(-381, -22.48) * mm, "end": v(-361.95, -22.48) * mm});
            skLineSegment(sketch, "E156.MirrorCS", {"start": v(-361.95, -22.48) * mm, "end": v(-361.95, -25.65) * mm});
            skLineSegment(sketch, "E157.MirrorCS", {"start": v(-381, -25.65) * mm, "end": v(-361.95, -25.65) * mm});
            skLineSegment(sketch, "E158.MirrorCS", {"start": v(-381, -22.48) * mm, "end": v(-381, -25.65) * mm});
            skLineSegment(sketch, "E159.MirrorCS", {"start": v(-349, 9.52) * mm, "end": v(-349, -9.52) * mm});
            skLineSegment(sketch, "E160.MirrorCS", {"start": v(-349, -9.53) * mm, "end": v(-345.82, -9.53) * mm});
            skLineSegment(sketch, "E161.MirrorCS", {"start": v(-345.82, 9.53) * mm, "end": v(-345.82, -9.53) * mm});
            skLineSegment(sketch, "E162.MirrorCS", {"start": v(-349, 9.53) * mm, "end": v(-345.82, 9.53) * mm});
            skLineSegment(sketch, "E163", {"start": v(-361.95, 25.65) * mm, "end": v(-345.82, 25.65) * mm, "construction": true});
            skLineSegment(sketch, "E164", {"start": v(-345.82, 25.65) * mm, "end": v(-345.82, 9.53) * mm, "construction": true});
            skLineSegment(sketch, "E165.MirrorCS", {"start": v(381, 22.48) * mm, "end": v(381, 25.65) * mm});
            skLineSegment(sketch, "E166.MirrorCS", {"start": v(381, 22.48) * mm, "end": v(361.95, 22.48) * mm});
            skLineSegment(sketch, "E167.MirrorCS", {"start": v(381, 25.65) * mm, "end": v(361.95, 25.65) * mm});
            skLineSegment(sketch, "E168.MirrorCS", {"start": v(361.95, 22.48) * mm, "end": v(361.95, 25.65) * mm});
            skLineSegment(sketch, "E169.MirrorCS", {"start": v(349, 9.53) * mm, "end": v(345.82, 9.53) * mm});
            skLineSegment(sketch, "E170.MirrorCS", {"start": v(349, 9.52) * mm, "end": v(349, -9.52) * mm});
            skLineSegment(sketch, "E171.MirrorCS", {"start": v(345.82, 9.53) * mm, "end": v(345.82, -9.53) * mm});
            skLineSegment(sketch, "E172.MirrorCS", {"start": v(349, -9.52) * mm, "end": v(345.82, -9.52) * mm});
            skLineSegment(sketch, "E173.MirrorCS", {"start": v(361.95, -22.48) * mm, "end": v(361.95, -25.65) * mm});
            skLineSegment(sketch, "E174.MirrorCS", {"start": v(381, -22.48) * mm, "end": v(361.95, -22.48) * mm});
            skLineSegment(sketch, "E175.MirrorCS", {"start": v(381, -25.65) * mm, "end": v(361.95, -25.65) * mm});
            skLineSegment(sketch, "E176.MirrorCS", {"start": v(381, -22.48) * mm, "end": v(381, -25.65) * mm});
            skLineSegment(sketch, "E177.MirrorCS", {"start": v(393.95, -9.52) * mm, "end": v(397.13, -9.52) * mm});
            skLineSegment(sketch, "E178.MirrorCS", {"start": v(393.95, 9.52) * mm, "end": v(393.95, -9.52) * mm});
            skLineSegment(sketch, "E179.MirrorCS", {"start": v(397.13, 9.53) * mm, "end": v(397.13, -9.53) * mm});
            skLineSegment(sketch, "E180.MirrorCS", {"start": v(393.95, 9.53) * mm, "end": v(397.13, 9.53) * mm});
            skPoint(sketch, "E181", {"position": v(-393.95, 44.66) * mm});
            skPoint(sketch, "E182.MirrorP", {"position": v(-393.95, -44.66) * mm});
            skSolve(sketch);
        }
        {
            var Q0;
            Q0 = qSketchRegion(id + "F4", true);
            extrude(context, id + "F5", {"entities" : qUnion([Q0]), "operationType" : NewBodyOperationType.REMOVE, "endBound" : BoundingType.THROUGH_ALL, "oppositeDirection" : true, "depth" : 25.4 * mm});
        }
        {
            var Q0;
            Q0=makeQuery(id+"F1.opExtrude","CAP_FACE",FACE,{"disambiguationData":[OSD([sQuery(id+"F0.wireOp",EDGE,"E2"),sQuery(id+"F0.wireOp",EDGE,"E3.0"),sQuery(id+"F0.wireOp",EDGE,"E4"),sQuery(id+"F0.wireOp",EDGE,"E6"),sQuery(id+"F0.wireOp",EDGE,"E7"),sQuery(id+"F0.wireOp",EDGE,"E8"),sQuery(id+"F0.wireOp",EDGE,"E9"),sQuery(id+"F0.wireOp",EDGE,"E10.MirrorCS"),sQuery(id+"F0.wireOp",EDGE,"E11.MirrorCS"),sQuery(id+"F0.wireOp",EDGE,"E12.MirrorCS"),sQuery(id+"F0.wireOp",EDGE,"E13.MirrorCS"),sQuery(id+"F0.wireOp",EDGE,"E14.MirrorCS"),sQuery(id+"F0.wireOp",EDGE,"E15.MirrorCS"),sQuery(id+"F0.wireOp",EDGE,"E16.MirrorCS"),sQuery(id+"F0.wireOp",EDGE,"E17.MirrorCS"),sQuery(id+"F0.wireOp",EDGE,"E18.MirrorCS"),sQuery(id+"F0.wireOp",EDGE,"E19.MirrorCS"),sQuery(id+"F0.wireOp",EDGE,"E20.MirrorCS"),sQuery(id+"F0.wireOp",EDGE,"E21.MirrorCS"),sQuery(id+"F0.wireOp",EDGE,"E22.MirrorCS"),sQuery(id+"F0.wireOp",EDGE,"E23.MirrorCS"),sQuery(id+"F0.wireOp",EDGE,"E24.MirrorCS"),sQuery(id+"F0.wireOp",EDGE,"E25.MirrorCS"),sQuery(id+"F0.wireOp",EDGE,"E26.MirrorCS"),sQuery(id+"F0.wireOp",EDGE,"E28"),sQuery(id+"F0.wireOp",EDGE,"E29"),sQuery(id+"F0.wireOp",EDGE,"E30"),sQuery(id+"F0.wireOp",EDGE,"E31"),sQuery(id+"F0.wireOp",EDGE,"E32"),sQuery(id+"F0.wireOp",EDGE,"E33"),sQuery(id+"F0.wireOp",EDGE,"E34"),sQuery(id+"F0.wireOp",EDGE,"E35.MirrorCS"),sQuery(id+"F0.wireOp",EDGE,"E36.MirrorCS"),sQuery(id+"F0.wireOp",EDGE,"E37.MirrorCS"),sQuery(id+"F0.wireOp",EDGE,"E38.MirrorCS"),sQuery(id+"F0.wireOp",EDGE,"E39.MirrorCS"),sQuery(id+"F0.wireOp",EDGE,"E40.MirrorCS"),sQuery(id+"F0.wireOp",EDGE,"E41.MirrorCS"),sQuery(id+"F0.wireOp",EDGE,"E42"),sQuery(id+"F0.wireOp",EDGE,"E43"),sQuery(id+"F0.wireOp",EDGE,"E44.trimOffspring"),sQuery(id+"F0.wireOp",EDGE,"E46.MirrorCS"),sQuery(id+"F0.wireOp",EDGE,"E47.MirrorCS"),sQuery(id+"F0.wireOp",EDGE,"E49.trimOffspring"),sQuery(id+"F0.wireOp",EDGE,"E50.filletArc"),sQuery(id+"F0.wireOp",EDGE,"E51.filletArc"),sQuery(id+"F0.wireOp",EDGE,"E52.filletArc"),sQuery(id+"F0.wireOp",EDGE,"E53.filletArc"),sQuery(id+"F0.wireOp",EDGE,"E54.filletArc"),sQuery(id+"F0.wireOp",EDGE,"E55.filletArc"),sQuery(id+"F0.wireOp",EDGE,"E56.filletArc"),sQuery(id+"F0.wireOp",EDGE,"E57.filletArc"),sQuery(id+"F0.wireOp",EDGE,"E58.filletArc"),sQuery(id+"F0.wireOp",EDGE,"E59.filletArc"),sQuery(id+"F0.wireOp",EDGE,"E60.filletArc"),sQuery(id+"F0.wireOp",EDGE,"E61.filletArc"),sQuery(id+"F0.wireOp",EDGE,"E62.filletArc"),sQuery(id+"F0.wireOp",EDGE,"E63.filletArc"),sQuery(id+"F0.wireOp",EDGE,"E64.filletArc"),sQuery(id+"F0.wireOp",EDGE,"E65.filletArc"),sQuery(id+"F0.wireOp",EDGE,"E66.filletArc"),sQuery(id+"F0.wireOp",EDGE,"E67.filletArc"),sQuery(id+"F0.wireOp",EDGE,"E68.filletArc"),sQuery(id+"F0.wireOp",EDGE,"E69.filletArc"),sQuery(id+"F0.wireOp",EDGE,"E70.filletArc"),sQuery(id+"F0.wireOp",EDGE,"E71.filletArc"),sQuery(id+"F0.wireOp",EDGE,"E72.filletArc"),sQuery(id+"F0.wireOp",EDGE,"E73.filletArc"),sQuery(id+"F0.wireOp",EDGE,"E74"),sQuery(id+"F0.wireOp",EDGE,"E75"),sQuery(id+"F0.wireOp",EDGE,"E76"),sQuery(id+"F0.wireOp",EDGE,"E77.filletArc"),sQuery(id+"F0.wireOp",EDGE,"E79.filletArc"),sQuery(id+"F0.wireOp",EDGE,"E81.MirrorCS"),sQuery(id+"F0.wireOp",EDGE,"E82.MirrorCS"),sQuery(id+"F0.wireOp",EDGE,"E83.MirrorCS"),sQuery(id+"F0.wireOp",EDGE,"E84.MirrorCS"),sQuery(id+"F0.wireOp",EDGE,"E85.MirrorCS"),sQuery(id+"F0.wireOp",EDGE,"E86.MirrorCS"),sQuery(id+"F0.wireOp",EDGE,"E87.MirrorCS"),sQuery(id+"F0.wireOp",EDGE,"E88.MirrorCS"),sQuery(id+"F0.wireOp",EDGE,"E89.MirrorCS"),sQuery(id+"F0.wireOp",EDGE,"E90.MirrorCS"),sQuery(id+"F0.wireOp",EDGE,"E91.MirrorCS"),sQuery(id+"F0.wireOp",EDGE,"E92.MirrorCS"),sQuery(id+"F0.wireOp",EDGE,"E93.MirrorCS"),sQuery(id+"F0.wireOp",EDGE,"E94.MirrorCS"),sQuery(id+"F0.wireOp",EDGE,"E95.MirrorCS"),sQuery(id+"F0.wireOp",EDGE,"E97"),sQuery(id+"F0.wireOp",EDGE,"E98"),sQuery(id+"F0.wireOp",EDGE,"E99.filletArc"),sQuery(id+"F0.wireOp",EDGE,"E100.MirrorCS"),sQuery(id+"F0.wireOp",EDGE,"E101.MirrorCS"),sQuery(id+"F0.wireOp",EDGE,"E102.MirrorCS"),sQuery(id+"F0.wireOp",EDGE,"E103.filletArc"),sQuery(id+"F0.wireOp",EDGE,"E104.MirrorCS"),sQuery(id+"F0.wireOp",EDGE,"E105.MirrorCS"),sQuery(id+"F0.wireOp",EDGE,"E106.MirrorCS"),sQuery(id+"F0.wireOp",EDGE,"E107.MirrorCS"),sQuery(id+"F0.wireOp",EDGE,"E108.MirrorCS"),sQuery(id+"F0.wireOp",EDGE,"E109.MirrorCS"),sQuery(id+"F0.wireOp",EDGE,"E110.MirrorCS")])],"isStart":false});
            var sketch = newSketch(context, id + "F6", { "sketchPlane" : qUnion([Q0])});
            skCircle(sketch, "E183", {"center": v(-371.48, 0) * mm, "radius": 12.7 * mm});
            skCircle(sketch, "E184", {"center": v(-355.98, 15.5) * mm, "radius": 1.79 * mm});
            skCircle(sketch, "E185", {"center": v(-355.98, -15.5) * mm, "radius": 1.79 * mm});
            skCircle(sketch, "E186", {"center": v(-386.97, -15.5) * mm, "radius": 1.79 * mm});
            skCircle(sketch, "E187", {"center": v(-386.97, 15.5) * mm, "radius": 1.79 * mm});
            skCircle(sketch, "E188", {"center": v(-371.48, 0) * mm, "radius": 21.9 * mm, "construction": true});
            skLineSegment(sketch, "E189", {"start": v(-386.97, 15.5) * mm, "end": v(-355.98, 15.5) * mm, "construction": true});
            skLineSegment(sketch, "E190", {"start": v(-355.98, -15.5) * mm, "end": v(-355.98, 15.5) * mm, "construction": true});
            skLineSegment(sketch, "E191", {"start": v(-355.98, -15.5) * mm, "end": v(-386.97, -15.5) * mm, "construction": true});
            skLineSegment(sketch, "E192", {"start": v(-386.97, -15.5) * mm, "end": v(-386.97, 15.5) * mm, "construction": true});
            skCircle(sketch, "E193.MirrorC", {"center": v(355.98, 15.5) * mm, "radius": 1.79 * mm});
            skCircle(sketch, "E194.MirrorC", {"center": v(371.48, 0) * mm, "radius": 12.7 * mm});
            skCircle(sketch, "E195.MirrorC", {"center": v(355.98, -15.5) * mm, "radius": 1.79 * mm});
            skCircle(sketch, "E196.MirrorC", {"center": v(386.97, -15.5) * mm, "radius": 1.79 * mm});
            skCircle(sketch, "E197.MirrorC", {"center": v(386.97, 15.5) * mm, "radius": 1.79 * mm});
            skSolve(sketch);
        }
        {
            var Q0;
            Q0 = qSketchRegion(id + "F6", true);
            extrude(context, id + "F7", {"entities" : qUnion([Q0]), "operationType" : NewBodyOperationType.REMOVE, "endBound" : BoundingType.THROUGH_ALL, "oppositeDirection" : true, "depth" : 25.4 * mm});
        }
    });
